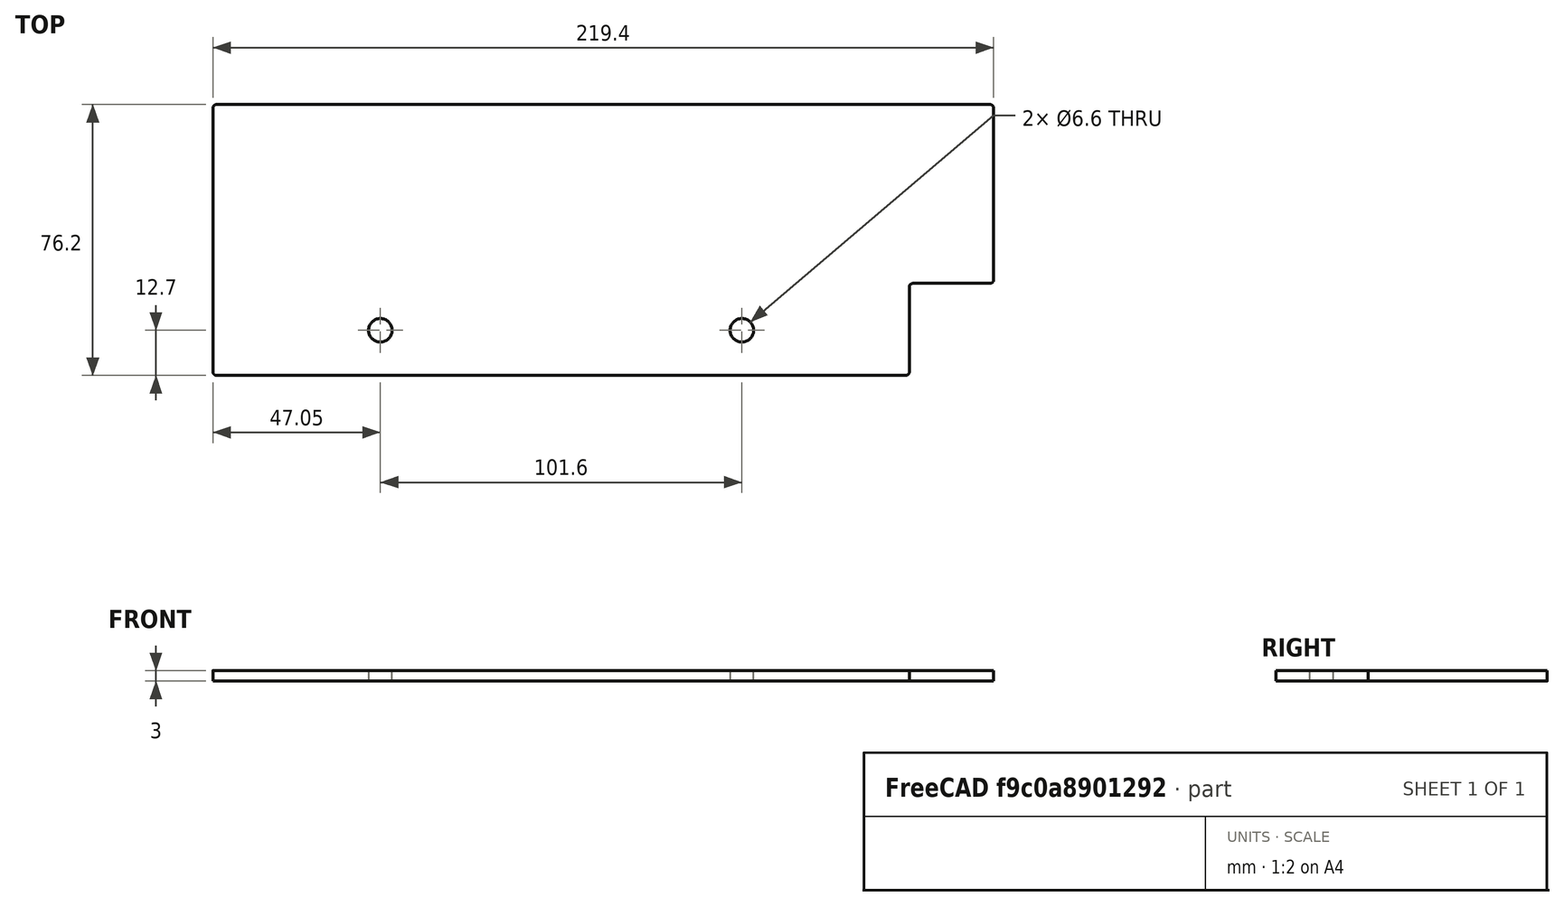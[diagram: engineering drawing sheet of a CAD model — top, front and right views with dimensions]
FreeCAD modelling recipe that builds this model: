
FCSTD DOCUMENT  (FreeCAD 0.20R29603 (Git))
Label: right_wall_back_24in
License: All rights reserved
LicenseURL: http://en.wikipedia.org/wiki/All_rights_reserved
objects: Spreadsheet::Sheet×1, Sketcher::SketchObject×1, PartDesign::Pad×1, PartDesign::Body×1
note: 4 computed .brp shape members not serialized (recipe doc carries the construction recipe); baked Part::Feature solids carry a one-line shape summary decoded from their .brp

FEATURE [Spreadsheet::Sheet] Spreadsheet
  cells = A2=Parameters; A3=DistanceBackToDoor; B3(DistanceBackToDoor)==219.9mm; A4=DistanceBackToBracket; B4(DistanceBackToBracket)==196.2mm; A5=LengthMargin; B5(LengthMargin)==0.5mm; A6=LengthBackToDoor; B6(LengthBackToDoor)==DistanceBackToDoor - LengthMargin; A7=LengthBackToBracket; B7(LengthBackToBracket)==DistanceBackToBracket - LengthMargin; A8=Height; B8(Height)==3in; A9=Thickness; B9(Thickness)==3mm; A10=CutoutMargin; B10(CutoutMargin)==0.5mm; A11=CutoutHeight; B11(CutoutHeight)==1in + CutoutMargin; A12=FilletRadius; B12(FilletRadius)==1mm; A13=MountHoleDiameter; B13(MountHoleDiameter)==0.26in; A14=MountHoleDistanceFromBottom; B14(MountHoleDistanceFromBottom)==0.5in; A15=MountHoleSpacing; B15(MountHoleSpacing)==2in
FEATURE [Sketcher::SketchObject] Sketch
  FullyConstrained = true
  MapMode = 5
  Support = -> [XY_Plane]
  expr: Constraints[14] = Spreadsheet.FilletRadius
  expr: Constraints[20] = Spreadsheet.Height
  expr: Constraints[44] = Spreadsheet.MountHoleDistanceFromBottom
  expr: Constraints[50] = Spreadsheet.MountHoleSpacing
  expr: Constraints[54] = Spreadsheet.MountHoleDiameter
  expr: Constraints[7] = Spreadsheet.LengthBackToDoor
  expr: Constraints[8] = Spreadsheet.LengthBackToBracket
  expr: Constraints[9] = Spreadsheet.CutoutHeight
  sketch-geometry (24):
    g0: LineSegment StartX=0 StartY=75.2 StartZ=0 EndX=0 EndY=1 EndZ=0
    g1: LineSegment StartX=1 StartY=1.6e-15 StartZ=0 EndX=194.7 EndY=1.6e-15 EndZ=0
    g2: LineSegment StartX=195.7 StartY=1 StartZ=0 EndX=195.7 EndY=24.9 EndZ=0
    g3: LineSegment StartX=196.7 StartY=25.9 StartZ=0 EndX=218.4 EndY=25.9 EndZ=0
    g4: LineSegment StartX=219.4 StartY=26.9 StartZ=0 EndX=219.4 EndY=75.2 EndZ=0
    g5: LineSegment StartX=218.4 StartY=76.2 StartZ=0 EndX=1 EndY=76.2 EndZ=0
    g6: ArcOfCircle CenterX=1 CenterY=75.2 CenterZ=0 NormalX=0 NormalY=0 NormalZ=1 AngleXU=0 Radius=1 StartAngle=1.5708 EndAngle=3.14159
    g7: GeomPoint X=0 Y=76.2 Z=0
    g8: ArcOfCircle CenterX=1 CenterY=1 CenterZ=0 NormalX=0 NormalY=0 NormalZ=1 AngleXU=0 Radius=1 StartAngle=3.14159 EndAngle=4.71239
    g9: GeomPoint X=0 Y=0 Z=0
    g10: ArcOfCircle CenterX=194.7 CenterY=1 CenterZ=0 NormalX=0 NormalY=0 NormalZ=1 AngleXU=0 Radius=1 StartAngle=4.71239 EndAngle=6.28319
    g11: GeomPoint X=195.7 Y=0 Z=0
    g12: ArcOfCircle CenterX=196.7 CenterY=24.9 CenterZ=0 NormalX=0 NormalY=0 NormalZ=1 AngleXU=0 Radius=1 StartAngle=1.5708 EndAngle=3.14159
    g13: GeomPoint X=195.7 Y=25.9 Z=0
    g14: ArcOfCircle CenterX=218.4 CenterY=26.9 CenterZ=0 NormalX=0 NormalY=0 NormalZ=1 AngleXU=0 Radius=1 StartAngle=4.71239 EndAngle=6.28319
    g15: GeomPoint X=219.4 Y=25.9 Z=0
    g16: ArcOfCircle CenterX=218.4 CenterY=75.2 CenterZ=0 NormalX=0 NormalY=0 NormalZ=1 AngleXU=0 Radius=1 StartAngle=-9e-16 EndAngle=1.5708
    g17: GeomPoint X=219.4 Y=76.2 Z=0
    g18: GeomPoint X=97.85 Y=0 Z=0
    g19: LineSegment StartX=97.85 StartY=0 StartZ=0 EndX=97.85 EndY=12.7 EndZ=0
    g20: LineSegment StartX=47.05 StartY=12.7 StartZ=0 EndX=97.85 EndY=12.7 EndZ=0
    g21: LineSegment StartX=97.85 StartY=12.7 StartZ=0 EndX=148.65 EndY=12.7 EndZ=0
    g22: Circle CenterX=47.05 CenterY=12.7 CenterZ=0 NormalX=0 NormalY=0 NormalZ=1 AngleXU=0 Radius=3.302
    g23: Circle CenterX=148.65 CenterY=12.7 CenterZ=0 NormalX=0 NormalY=0 NormalZ=1 AngleXU=0 Radius=3.302
  constraints (55):
    c: Vertical(g0)
    c: Horizontal(g1)
    c: Vertical(g2)
    c: Horizontal(g3)
    c: Vertical(g4)
    c: Horizontal(g5)
    c: Coincident(g-1,g9)
    c: DistanceX(g7,g17) = 219.4
    c: DistanceX(g9,g11) = 195.7
    c: DistanceY(g11,g13) = 25.9
    c: PointOnObject(g7,g0)
    c: PointOnObject(g7,g5)
    c: Tangent(g0,g6) = -1.5708
    c: Tangent(g5,g6) = -1.5708
    c: Radius(g6) = 1
    c: PointOnObject(g9,g0)
    c: PointOnObject(g9,g1)
    c: Tangent(g0,g8) = -1.5708
    c: Tangent(g1,g8) = -1.5708
    c: Equal(g8,g6)
    c: DistanceY(g1,g5) = 76.2
    c: PointOnObject(g11,g1)
    c: PointOnObject(g11,g2)
    c: Tangent(g1,g10) = -1.5708
    c: Tangent(g2,g10) = -1.5708
    c: Equal(g10,g8)
    c: PointOnObject(g13,g2)
    c: PointOnObject(g13,g3)
    c: Tangent(g2,g12) = 1.5708
    c: Tangent(g3,g12) = 1.5708
    c: Equal(g12,g10)
    c: PointOnObject(g15,g3)
    c: PointOnObject(g15,g4)
    c: Tangent(g3,g14) = -1.5708
    c: Tangent(g4,g14) = -1.5708
    c: Equal(g14,g12)
    c: PointOnObject(g17,g5)
    c: PointOnObject(g17,g4)
    c: Tangent(g5,g16) = -1.5708
    c: Tangent(g4,g16) = -1.5708
    c: Equal(g16,g14)
    c: Symmetric(g1,g1,g18)
    c: Coincident(g19,g18)
    c: Vertical(g19)
    c: DistanceY(g19,g19) = 12.7
    c: Horizontal(g20)
    c: Coincident(g20,g21)
    c: Horizontal(g21)
    c: Equal(g20,g21)
    c: Coincident(g19,g20)
    c: DistanceX(g20,g20) = 50.8
    c: Coincident(g22,g20)
    c: Coincident(g23,g21)
    c: Equal(g23,g22)
    c: Diameter(g23) = 6.604
FEATURE [PartDesign::Pad] Pad
  Direction = (0,0,1)
  Length = 3
  Length2 = 10
  Profile = -> Sketch
  ReferenceAxis = -> Sketch [N_Axis]
  Type = 0
  expr: Length = Spreadsheet.Thickness
FEATURE [PartDesign::Body] Body
  Group = -> [Sketch,Pad]
  Origin = -> Origin
  Tip = -> Pad
